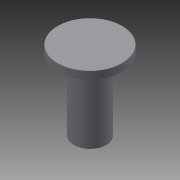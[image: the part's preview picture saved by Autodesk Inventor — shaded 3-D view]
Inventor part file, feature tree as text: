
AUTODESK INVENTOR PART (.ipt)
format: ipt  version: 2015 (Build 190159000, 159)  size: 83,968 bytes
history: native  units: in
note: dims shown in document units (in); Inventor stores cm internally (conversion verified against a paired STEP export)
features: revolve x1, chamfer x1, sketch x1
ambient origin geometry x8: Origin, YZ Plane, XZ Plane, XY Plane, X Axis, Y Axis, Z Axis, Center Point
bodies: Solid1 (feature_tree)
feature tree (3):
  revolve  "Revolution1"  [1 undecoded]
  chamfer  "Chamfer1"  Distance=1.0625in
  sketch  "Sketch1"  dims[d0=2.1181in d1=5.1811in d2=1.0625in d3=90.0deg d4=0.5in d5=0.0197in d6=0.0787in d7=45.0deg]
note: 1 required parameter value undecoded (feature->parameter linkage not recoverable at this tier; creation-order binding heuristic only, values carry confidence <= 0.55)
